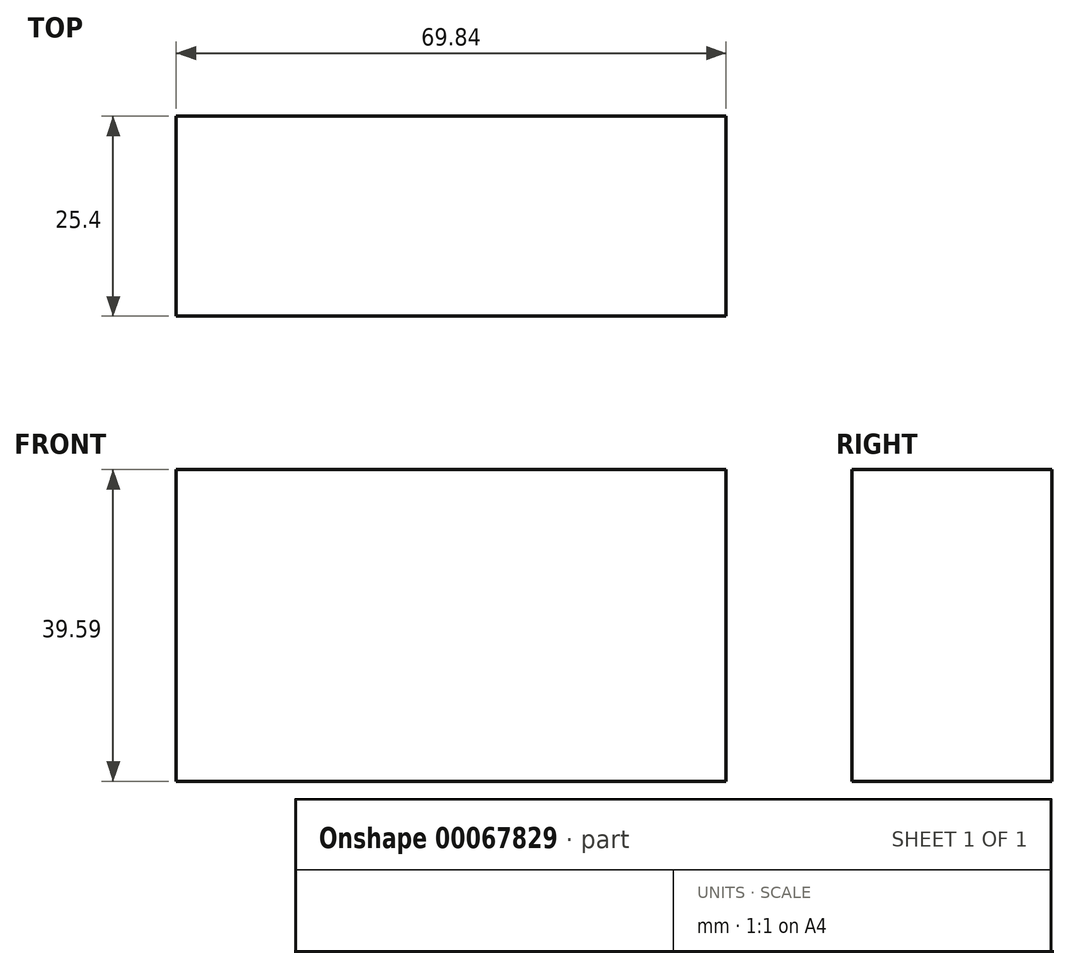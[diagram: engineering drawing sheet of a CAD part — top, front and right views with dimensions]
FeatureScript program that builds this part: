
annotation { "Feature Type Name" : "Feature", "Feature Type Description" : "" }
export const myFeature = defineFeature(function(context is Context, id is Id, definition is map)
    precondition{}
    {
        {
            var Q0;
            Q0=qCreatedBy(makeId("Front.planeOp"),FACE);
            var sketch = newSketch(context, id + "F0", { "sketchPlane" : qUnion([Q0])});
            skLineSegment(sketch, "E0.bottom", {"start": v(0, 0) * mm, "end": v(69.84, 0) * mm});
            skLineSegment(sketch, "E0.top", {"start": v(0, 39.59) * mm, "end": v(69.84, 39.59) * mm});
            skLineSegment(sketch, "E0.left", {"start": v(0, 0) * mm, "end": v(0, 39.59) * mm});
            skLineSegment(sketch, "E0.right", {"start": v(69.84, 0) * mm, "end": v(69.84, 39.59) * mm});
            skSolve(sketch);
        }
        {
            var Q0;
            Q0=makeQuery(id+"F0.imprint","IMPRINT",FACE,{"disambiguationData":[TD([[makeQuery(id+"F0.imprint","IMPRINT",EDGE,{"derivedFrom":sQuery(id+"F0.wireOp",EDGE,"E0.bottom")}),1.0]])]});
            extrude(context, id + "F1", {"entities" : qUnion([Q0]), "depth" : 25.4 * mm});
        }
    });
